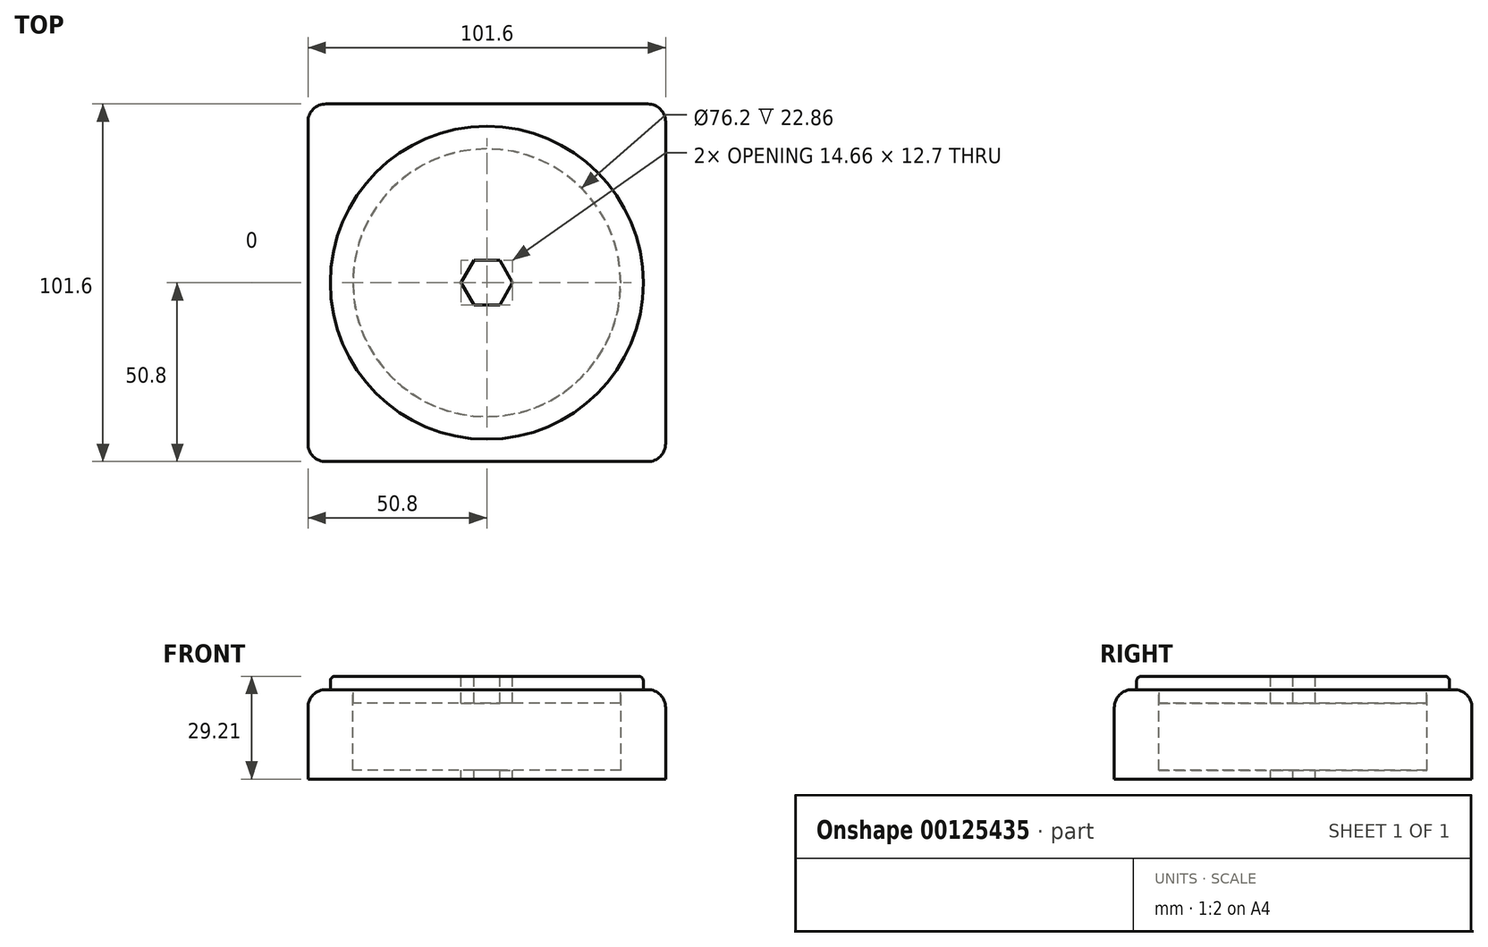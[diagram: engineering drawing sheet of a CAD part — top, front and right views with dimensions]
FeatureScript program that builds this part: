
annotation { "Feature Type Name" : "Feature", "Feature Type Description" : "" }
export const myFeature = defineFeature(function(context is Context, id is Id, definition is map)
    precondition{}
    {
        {
            var Q0;
            Q0=qCreatedBy(makeId("Top.planeOp"),FACE);
            var sketch = newSketch(context, id + "F0", { "sketchPlane" : qUnion([Q0])});
            skLineSegment(sketch, "E0.bottom", {"start": v(50.8, 50.8) * mm, "end": v(-50.8, 50.8) * mm});
            skLineSegment(sketch, "E0.top", {"start": v(50.8, -50.8) * mm, "end": v(-50.8, -50.8) * mm});
            skLineSegment(sketch, "E0.left", {"start": v(50.8, 50.8) * mm, "end": v(50.8, -50.8) * mm});
            skLineSegment(sketch, "E0.right", {"start": v(-50.8, 50.8) * mm, "end": v(-50.8, -50.8) * mm});
            skPoint(sketch, "E0.middle", {"position": v(0, 0) * mm});
            skSolve(sketch);
        }
        {
            var Q0;
            Q0=makeQuery(id+"F0.imprint","IMPRINT",FACE,{"disambiguationData":[TD([[makeQuery(id+"F0.imprint","IMPRINT",EDGE,{"derivedFrom":sQuery(id+"F0.wireOp",EDGE,"E0.bottom")}),1.0]])]});
            extrude(context, id + "F1", {"entities" : qUnion([Q0]), "depth" : 25.4 * mm});
        }
        {
            var Q0;
            Q0=makeQuery(id+"F1.opExtrude","CAP_FACE",FACE,{"disambiguationData":[OSD([sQuery(id+"F0.wireOp",EDGE,"E0.bottom"),sQuery(id+"F0.wireOp",EDGE,"E0.top"),sQuery(id+"F0.wireOp",EDGE,"E0.left"),sQuery(id+"F0.wireOp",EDGE,"E0.right")])],"isStart":false});
            var sketch = newSketch(context, id + "F2", { "sketchPlane" : qUnion([Q0])});
            skCircle(sketch, "E1", {"center": v(0, 0) * mm, "radius": 38.1 * mm});
            skSolve(sketch);
        }
        {
            var Q0;
            Q0=makeQuery(id+"F2.imprint","IMPRINT",FACE,{"disambiguationData":[TD([[makeQuery(id+"F2.imprint","IMPRINT",EDGE,{"derivedFrom":sQuery(id+"F2.wireOp",EDGE,"E1")}),1.0]])]});
            extrude(context, id + "F3", {"entities" : qUnion([Q0]), "operationType" : NewBodyOperationType.REMOVE, "oppositeDirection" : true, "depth" : 22.86 * mm});
        }
        {
            var Q0;
            Q0=makeQuery(id+"F1.opExtrude","CAP_FACE",FACE,{"disambiguationData":[OSD([sQuery(id+"F0.wireOp",EDGE,"E0.bottom"),sQuery(id+"F0.wireOp",EDGE,"E0.top"),sQuery(id+"F0.wireOp",EDGE,"E0.left"),sQuery(id+"F0.wireOp",EDGE,"E0.right")])],"isStart":false});
            var sketch = newSketch(context, id + "F4", { "sketchPlane" : qUnion([Q0])});
            skCircle(sketch, "E2", {"center": v(0, 0) * mm, "radius": 37.97 * mm});
            skSolve(sketch);
        }
        {
            var Q0;
            Q0=makeQuery(id+"F4.imprint","IMPRINT",FACE,{"disambiguationData":[TD([[makeQuery(id+"F4.imprint","IMPRINT",EDGE,{"derivedFrom":sQuery(id+"F4.wireOp",EDGE,"E2")}),1.0]])]});
            extrude(context, id + "F5", {"entities" : qUnion([Q0]), "oppositeDirection" : true, "depth" : 3.8 * mm});
        }
        {
            var Q0;
            Q0=makeQuery(id+"F4.imprint","IMPRINT",FACE,{"disambiguationData":[TD([[makeQuery(id+"F4.imprint","IMPRINT",EDGE,{"derivedFrom":sQuery(id+"F4.wireOp",EDGE,"E2")}),1.0]])]});
            var sketch = newSketch(context, id + "F6", { "sketchPlane" : qUnion([Q0])});
            skCircle(sketch, "E3", {"center": v(0, 0) * mm, "radius": 44.45 * mm});
            skSolve(sketch);
        }
        {
            var Q0;
            Q0=makeQuery(id+"F6.imprint","IMPRINT",FACE,{"disambiguationData":[TD([[makeQuery(id+"F6.imprint","IMPRINT",EDGE,{"derivedFrom":sQuery(id+"F6.wireOp",EDGE,"E3")}),1.0]])]});
            var Q1;
            Q1=makeQuery(id+"F6.imprint","IMPRINT",FACE,{"disambiguationData":[TD([[makeQuery(id+"F6.imprint","IMPRINT",EDGE,{"derivedFrom":makeQuery(id+"F4.imprint","IMPRINT",EDGE,{"derivedFrom":sQuery(id+"F4.wireOp",EDGE,"E2")})}),1.0]])]});
            extrude(context, id + "F7", {"entities" : qUnion([Q0, Q1]), "operationType" : NewBodyOperationType.ADD, "depth" : 3.8 * mm});
        }
        {
            var Q0;
            Q0=makeQuery(id+"F1.opExtrude","SWEPT_EDGE",EDGE,{"disambiguationData":[OSD([sQuery(id+"F0.wireOp",EDGE,"E0.top"),sQuery(id+"F0.wireOp",EDGE,"E0.right")])]});
            var Q1;
            Q1=makeQuery(id+"F1.opExtrude","SWEPT_EDGE",EDGE,{"disambiguationData":[OSD([sQuery(id+"F0.wireOp",EDGE,"E0.top"),sQuery(id+"F0.wireOp",EDGE,"E0.left")])]});
            var Q2;
            Q2=makeQuery(id+"F1.opExtrude","SWEPT_EDGE",EDGE,{"disambiguationData":[OSD([sQuery(id+"F0.wireOp",EDGE,"E0.bottom"),sQuery(id+"F0.wireOp",EDGE,"E0.left")])]});
            var Q3;
            Q3=makeQuery(id+"F1.opExtrude","SWEPT_EDGE",EDGE,{"disambiguationData":[OSD([sQuery(id+"F0.wireOp",EDGE,"E0.bottom"),sQuery(id+"F0.wireOp",EDGE,"E0.right")])]});
            var Q4;
            Q4=makeQuery(id+"F1.opExtrude","CAP_EDGE",EDGE,{"disambiguationData":[OSD([sQuery(id+"F0.wireOp",EDGE,"E0.bottom")])],"isStart":false});
            var Q5;
            Q5=makeQuery(id+"F1.opExtrude","CAP_EDGE",EDGE,{"disambiguationData":[OSD([sQuery(id+"F0.wireOp",EDGE,"E0.right")])],"isStart":false});
            var Q6;
            Q6=makeQuery(id+"F1.opExtrude","CAP_EDGE",EDGE,{"disambiguationData":[OSD([sQuery(id+"F0.wireOp",EDGE,"E0.left")])],"isStart":false});
            var Q7;
            Q7=makeQuery(id+"F1.opExtrude","CAP_EDGE",EDGE,{"disambiguationData":[OSD([sQuery(id+"F0.wireOp",EDGE,"E0.top")])],"isStart":false});
            fillet(context, id + "F8", {"entities" : qUnion([Q0, Q1, Q2, Q3, Q4, Q5, Q6, Q7]), "radius" : 5.08 * mm, "tangentPropagation" : true, "allowEdgeOverflow" : false});
        }
        {
            var Q0;
            Q0=makeQuery(id+"F7.opExtrude","CAP_EDGE",EDGE,{"disambiguationData":[OSD([sQuery(id+"F6.wireOp",EDGE,"E3")])],"isStart":false});
            fillet(context, id + "F9", {"entities" : qUnion([Q0]), "radius" : 1.27 * mm, "tangentPropagation" : true, "allowEdgeOverflow" : false});
        }
        {
            var Q0;
            Q0=qCreatedBy(makeId("Top.planeOp"),FACE);
            cPlane(context, id + "F10", {"entities" : qUnion([Q0]), "cplaneType" : CPlaneType.OFFSET, "offset" : 127 * mm, "width" : 152.4 * mm, "height" : 152.4 * mm});
        }
        {
            var Q0;
            Q0=qCreatedBy(id+"F10.planeOp",FACE);
            var sketch = newSketch(context, id + "F11", { "sketchPlane" : qUnion([Q0])});
            skCircle(sketch, "E4.cCircle", {"center": v(0, 0) * mm, "radius": 6.35 * mm, "construction": true});
            skLineSegment(sketch, "E4.0", {"start": v(-3.67, 6.35) * mm, "end": v(3.67, 6.35) * mm});
            skLineSegment(sketch, "E4.1", {"start": v(3.67, 6.35) * mm, "end": v(7.33, 0) * mm});
            skLineSegment(sketch, "E4.2", {"start": v(7.33, 0) * mm, "end": v(3.67, -6.35) * mm});
            skLineSegment(sketch, "E4.3", {"start": v(3.67, -6.35) * mm, "end": v(-3.67, -6.35) * mm});
            skLineSegment(sketch, "E4.4", {"start": v(-3.67, -6.35) * mm, "end": v(-7.33, 0) * mm});
            skLineSegment(sketch, "E4.5", {"start": v(-7.33, 0) * mm, "end": v(-3.67, 6.35) * mm});
            skPoint(sketch, "E4.0.midPoint", {"position": v(0, 6.35) * mm});
            skSolve(sketch);
        }
        {
            var Q0;
            Q0=makeQuery(id+"F11.imprint","IMPRINT",FACE,{"disambiguationData":[TD([[makeQuery(id+"F11.imprint","IMPRINT",EDGE,{"derivedFrom":sQuery(id+"F11.wireOp",EDGE,"E4.0")}),-1.0]])]});
            extrude(context, id + "F12", {"entities" : qUnion([Q0]), "oppositeDirection" : true, "depth" : 248.92 * mm});
        }
        {
            var Q0;
            Q0=makeQuery(id+"F12.opExtrude","SWEPT_BODY",BODY,{"disambiguationData":[OSD([sQuery(id+"F11.wireOp",EDGE,"E4.0"),sQuery(id+"F11.wireOp",EDGE,"E4.1"),sQuery(id+"F11.wireOp",EDGE,"E4.2"),sQuery(id+"F11.wireOp",EDGE,"E4.3"),sQuery(id+"F11.wireOp",EDGE,"E4.4"),sQuery(id+"F11.wireOp",EDGE,"E4.5")])]});
            var Q1;
            Q1=makeQuery(id+"F1.opExtrude","SWEPT_BODY",BODY,{"disambiguationData":[OSD([sQuery(id+"F0.wireOp",EDGE,"E0.bottom"),sQuery(id+"F0.wireOp",EDGE,"E0.top"),sQuery(id+"F0.wireOp",EDGE,"E0.left"),sQuery(id+"F0.wireOp",EDGE,"E0.right")])]});
            var Q2;
            Q2=makeQuery(id+"F5.opExtrude","SWEPT_BODY",BODY,{"disambiguationData":[OSD([sQuery(id+"F4.wireOp",EDGE,"E2")])]});
            booleanBodies(context, id + "F13", {"operationType" : BooleanOperationType.SUBTRACTION, "tools" : qUnion([Q0]), "targets" : qUnion([Q1, Q2])});
        }
    });
